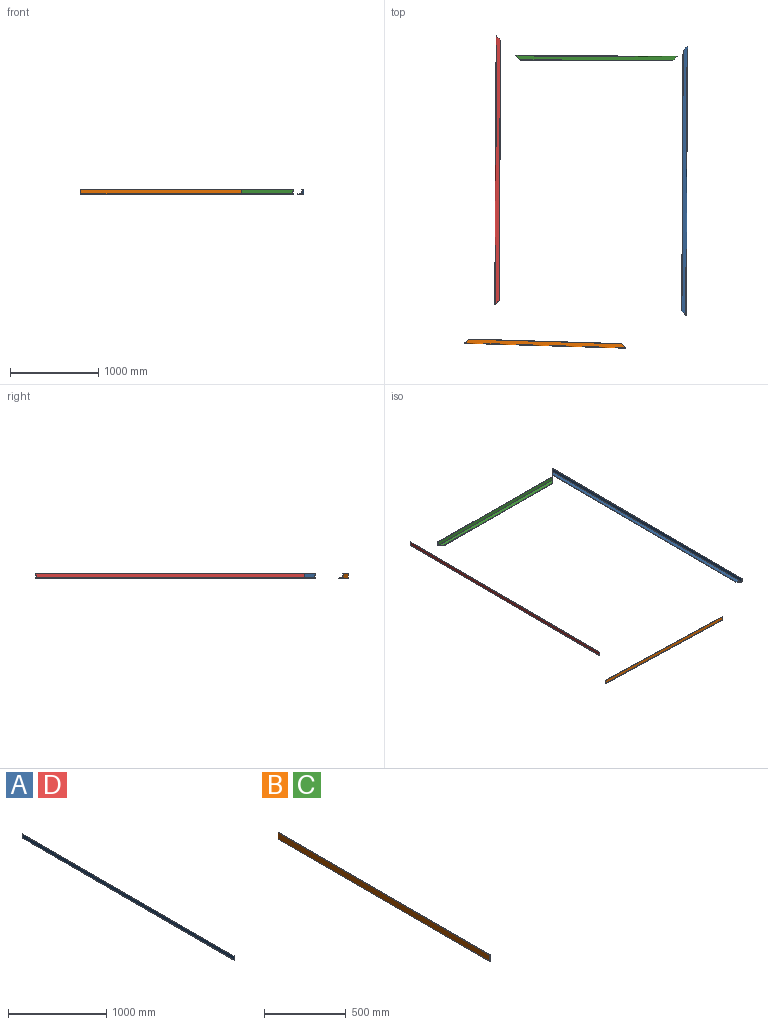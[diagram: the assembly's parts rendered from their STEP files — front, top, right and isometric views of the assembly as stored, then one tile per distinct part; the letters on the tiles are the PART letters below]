
ASSEMBLY  parts=4 mates=2
PART A: 9 faces, bbox 50.8x3048x50.8 mm
  f0: cylinder r=2.38mm len=3048mm, axis (0,1,0), area 22766.2mm2, adj f5,f6,f7,f8
  f1: cylinder r=2.38mm len=3048mm, axis (0,1,0), area 11394.4mm2, adj f2,f6,f7,f8
  f2: plane 3043.24x46.04mm, normal (0,0,-1), area 137983.6mm2, adj f1,f3,f7,f8
  f3: cylinder r=2.38mm len=2951.16mm, axis (0,1,0), area 22054.7mm2, adj f2,f4,f7,f8
  f4: plane 3038.48x43.66mm, normal (0,0,1), area 130742.6mm2, adj f3,f5,f7,f8
  f5: plane 3038.48x43.66mm, normal (1,0,0), area 132648.4mm2, adj f0,f4,f7,f8
  f6: plane 3048x46.04mm, normal (-1,0,0), area 140322.3mm2, adj f0,f1,f7,f8
  f7: plane 50.8x50.8mm, normal (0.71,-0.71,0), area 643.6mm2, adj f0,f1,f2,f3,f4,f5,f6
  f8: plane 50.8x50.8mm, normal (0.71,0.71,0), area 643.6mm2, adj f0,f1,f2,f3,f4,f5,f6
PART B: 9 faces, bbox 50.8x1828.8x50.8 mm
  f0: cylinder r=2.38mm len=1828.8mm, axis (0,1,0), area 13645.5mm2, adj f5,f6,f7,f8
  f1: cylinder r=2.38mm len=1828.8mm, axis (0,1,0), area 6834.1mm2, adj f2,f6,f7,f8
  f2: plane 1824.04x46.04mm, normal (0,0,-1), area 81854.7mm2, adj f1,f3,f7,f8
  f3: cylinder r=2.38mm len=1731.96mm, axis (0,1,0), area 12934mm2, adj f2,f4,f7,f8
  f4: plane 1819.28x43.66mm, normal (0,0,1), area 77516.9mm2, adj f3,f5,f7,f8
  f5: plane 1819.28x43.66mm, normal (1,0,0), area 79422.7mm2, adj f0,f4,f7,f8
  f6: plane 1828.8x46.04mm, normal (-1,0,0), area 84193.4mm2, adj f0,f1,f7,f8
  f7: plane 50.8x50.8mm, normal (0.71,-0.71,0), area 643.6mm2, adj f0,f1,f2,f3,f4,f5,f6
  f8: plane 50.8x50.8mm, normal (0.71,0.71,0), area 643.6mm2, adj f0,f1,f2,f3,f4,f5,f6
PART C: same geometry as B
PART D: same geometry as A
PLACE A rot(axis=(0,0,1),179.7deg) t=(2141.31,-3170.09,0)mm
PLACE B rot(axis=(0,0,1),88.3deg) t=(-366.57,-3486.01,0)mm
PLACE C rot(axis=(0,0,-1),90.3deg) t=(2041.73,-240.56,0)mm
PLACE D rot(axis=(0,0,-1),0.3deg) t=(-5.76,-5.71,0)mm
MATE planar C.f8 <-> A.f7  axis (0.7,-0.71,0) through (2027.3,-252.48,11.99)mm
MATE planar C.f7 <-> D.f8  axis (-0.71,-0.7,0) through (227.26,-243.47,11.99)mm
